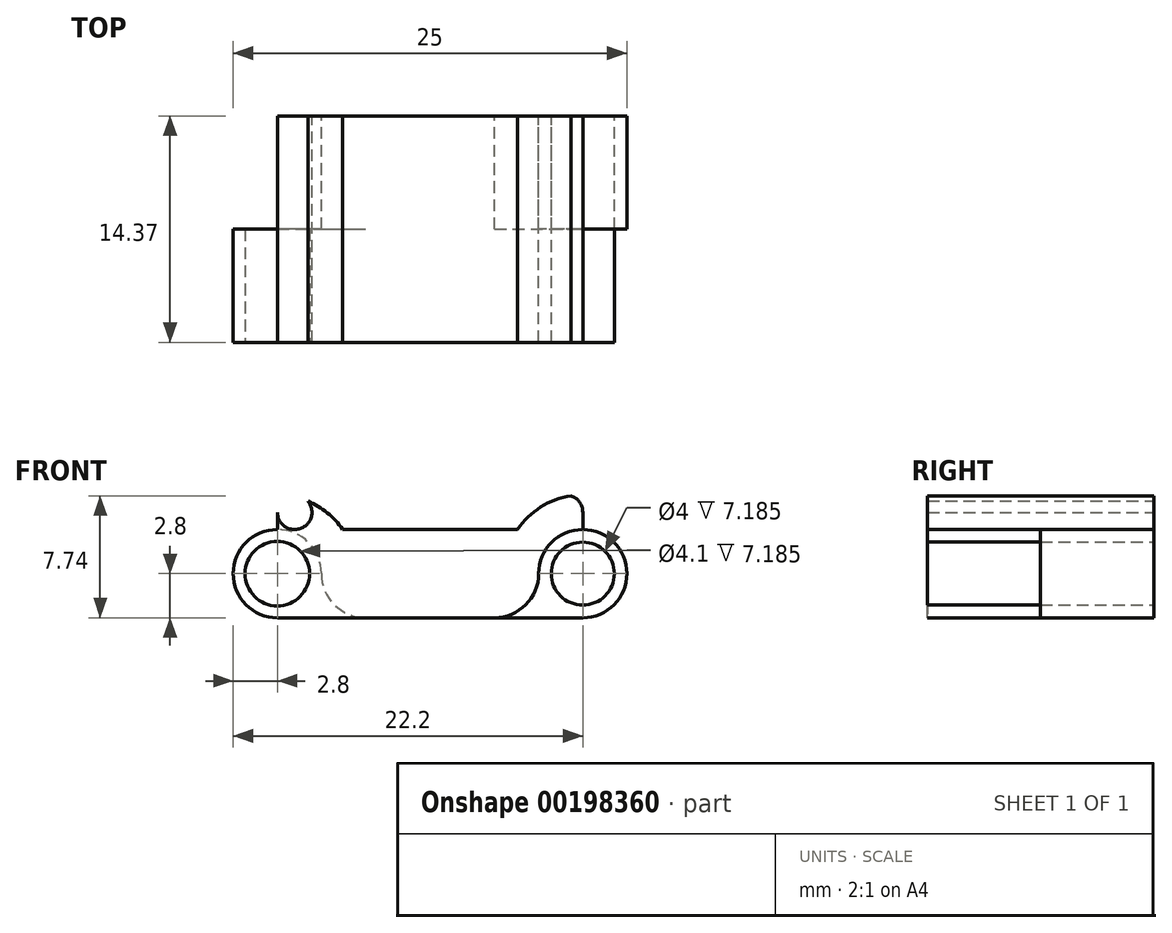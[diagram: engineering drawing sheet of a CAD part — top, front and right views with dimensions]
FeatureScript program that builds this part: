
annotation { "Feature Type Name" : "Feature", "Feature Type Description" : "" }
export const myFeature = defineFeature(function(context is Context, id is Id, definition is map)
    precondition{}
    {
        {
            var Q0;
            Q0=qCreatedBy(makeId("Front.planeOp"),FACE);
            var sketch = newSketch(context, id + "F0", { "sketchPlane" : qUnion([Q0])});
            skLineSegment(sketch, "E0.bottom", {"start": v(2.8, 0) * mm, "end": v(22.2, 0) * mm});
            skLineSegment(sketch, "E0.top", {"start": v(2.8, 5.6) * mm, "end": v(21.1, 5.6) * mm});
            skLineSegment(sketch, "E1.bottom", {"start": v(21.1, 5.6) * mm, "end": v(19.4, 5.6) * mm, "construction": true});
            skLineSegment(sketch, "E1.top", {"start": v(22.2, 0) * mm, "end": v(19.4, 0) * mm, "construction": true});
            skLineSegment(sketch, "E1.right", {"start": v(19.4, 5.6) * mm, "end": v(19.4, 0) * mm, "construction": true});
            skLineSegment(sketch, "E2", {"start": v(19.4, 5.6) * mm, "end": v(25, 0) * mm, "construction": true});
            skCircle(sketch, "E3", {"center": v(22.2, 2.8) * mm, "radius": 2.8 * mm});
            skCircle(sketch, "E4", {"center": v(22.2, 2.8) * mm, "radius": 2 * mm});
            skArc(sketch, "E5", {"start": v(21.45, 7.74) * mm, "mid": v(19.53, 7.03) * mm, "end": v(18.06, 5.6) * mm});
            skArc(sketch, "E6", {"start": v(17.74, 5.05) * mm, "mid": v(20.28, 0.14) * mm, "end": v(19.4, 5.6) * mm, "construction": true});
            skArc(sketch, "E7", {"start": v(16.6, 0) * mm, "mid": v(18.58, 0.82) * mm, "end": v(19.4, 2.8) * mm});
            skLineSegment(sketch, "E8", {"start": v(12.5, 5.6) * mm, "end": v(12.5, 0) * mm, "construction": true});
            skLineSegment(sketch, "E9", {"start": v(22.2, 2.8) * mm, "end": v(22.2, 6.7) * mm, "construction": true});
            skLineSegment(sketch, "E10", {"start": v(22.2, 6.7) * mm, "end": v(22.2, 5.6) * mm});
            skCircle(sketch, "E11", {"center": v(22.2, 6.7) * mm, "radius": 1.1 * mm, "construction": true});
            skArc(sketch, "E12", {"start": v(20.26, 7.4) * mm, "mid": v(21.4, 5.64) * mm, "end": v(21.45, 7.74) * mm});
            skPoint(sketch, "E13.orphan", {"position": v(22.2, 7.8) * mm});
            skPoint(sketch, "E14.orphan", {"position": v(25, 5.6) * mm});
            skArc(sketch, "E15.trimOffspring", {"start": v(17.74, 0.55) * mm, "mid": v(17.8, 0.42) * mm, "end": v(17.87, 0.3) * mm});
            skArc(sketch, "E16.MirrorCS", {"start": v(7.26, 0.55) * mm, "mid": v(7.2, 0.42) * mm, "end": v(7.13, 0.3) * mm});
            skLineSegment(sketch, "E17.MirrorCS", {"start": v(2.8, 6.7) * mm, "end": v(2.8, 5.6) * mm});
            skLineSegment(sketch, "E18.MirrorCS", {"start": v(2.8, 2.8) * mm, "end": v(2.8, 6.7) * mm, "construction": true});
            skCircle(sketch, "E19.MirrorC", {"center": v(2.8, 6.7) * mm, "radius": 1.1 * mm, "construction": true});
            skLineSegment(sketch, "E20.MirrorCS", {"start": v(3.9, 5.6) * mm, "end": v(5.6, 5.6) * mm, "construction": true});
            skPoint(sketch, "E21.MirrorP", {"position": v(0, 5.6) * mm});
            skPoint(sketch, "E22.MirrorP", {"position": v(2.8, 7.8) * mm});
            skLineSegment(sketch, "E23.MirrorCS", {"start": v(2.8, 0) * mm, "end": v(5.6, 0) * mm, "construction": true});
            skLineSegment(sketch, "E24.MirrorCS", {"start": v(5.6, 5.6) * mm, "end": v(0, 0) * mm, "construction": true});
            skLineSegment(sketch, "E25.MirrorCS", {"start": v(5.6, 5.6) * mm, "end": v(5.6, 0) * mm, "construction": true});
            skArc(sketch, "E26.MirrorCS", {"start": v(4.74, 7.4) * mm, "mid": v(3.6, 5.64) * mm, "end": v(3.55, 7.74) * mm});
            skArc(sketch, "E27.MirrorCS", {"start": v(7.26, 5.05) * mm, "mid": v(4.72, 0.14) * mm, "end": v(5.6, 5.6) * mm, "construction": true});
            skArc(sketch, "E28.MirrorCS", {"start": v(3.55, 7.74) * mm, "mid": v(5.47, 7.03) * mm, "end": v(6.94, 5.6) * mm});
            skCircle(sketch, "E29.MirrorC", {"center": v(2.8, 2.8) * mm, "radius": 2.8 * mm});
            skArc(sketch, "E30.MirrorCS", {"start": v(8.4, 0) * mm, "mid": v(6.42, 0.82) * mm, "end": v(5.6, 2.8) * mm});
            skCircle(sketch, "E31.MirrorC", {"center": v(2.8, 2.8) * mm, "radius": 2 * mm});
            skPoint(sketch, "E32.orphan", {"position": v(0, 0) * mm});
            skSolve(sketch);
        }
        {
            var Q0;
            {var subQ0=sQuery(id+"F0.wireOp",EDGE,"E10");Q0=makeQuery(id+"F0.imprint","IMPRINT",FACE,{"disambiguationData":[TD([[makeQuery(id+"F0.imprint","IMPRINT",EDGE,{"derivedFrom":subQ0}),-1.0]])]});}
            var Q1;
            {var subQ0=sQuery(id+"F0.wireOp",EDGE,"E12");var subQ1=sQuery(id+"F0.wireOp",EDGE,"E0.top");var subQ2=makeQuery(id+"F0.imprint","INTERSECT",VERTEX,{"derivedFrom":[subQ1,subQ0]});Q1=makeQuery(id+"F0.imprint","IMPRINT",FACE,{"disambiguationData":[TD([[makeQuery(id+"F0.imprint","IMPRINT",EDGE,{"disambiguationData":[TD([[subQ2,1.0]])],"derivedFrom":subQ1}),1.0]])]});}
            var Q2;
            {var subQ0=sQuery(id+"F0.wireOp",EDGE,"E12");var subQ1=sQuery(id+"F0.wireOp",EDGE,"E5");var subQ2=makeQuery(id+"F0.imprint","INTERSECT",VERTEX,{"disambiguationData":[OD(0.0)],"derivedFrom":[subQ1,subQ0]});Q2=makeQuery(id+"F0.imprint","IMPRINT",FACE,{"disambiguationData":[TD([[makeQuery(id+"F0.imprint","IMPRINT",EDGE,{"disambiguationData":[TD([[subQ2,-1.0]])],"derivedFrom":subQ1}),1.0]])]});}
            var Q3;
            {var subQ0=sQuery(id+"F0.wireOp",EDGE,"E28.MirrorCS");var subQ1=sQuery(id+"F0.wireOp",EDGE,"E0.top");var subQ2=makeQuery(id+"F0.imprint","INTERSECT",VERTEX,{"derivedFrom":[subQ1,subQ0]});Q3=makeQuery(id+"F0.imprint","IMPRINT",FACE,{"disambiguationData":[TD([[makeQuery(id+"F0.imprint","IMPRINT",EDGE,{"disambiguationData":[TD([[subQ2,1.0]])],"derivedFrom":subQ1}),1.0]])]});}
            var Q4;
            {var subQ0=sQuery(id+"F0.wireOp",EDGE,"E28.MirrorCS");var subQ1=sQuery(id+"F0.wireOp",EDGE,"E26.MirrorCS");var subQ2=makeQuery(id+"F0.imprint","INTERSECT",VERTEX,{"disambiguationData":[OD(0.0)],"derivedFrom":[subQ1,subQ0]});Q4=makeQuery(id+"F0.imprint","IMPRINT",FACE,{"disambiguationData":[TD([[makeQuery(id+"F0.imprint","IMPRINT",EDGE,{"disambiguationData":[TD([[subQ2,-1.0]])],"derivedFrom":subQ1}),-1.0]])]});}
            var Q5;
            {var subQ0=sQuery(id+"F0.wireOp",EDGE,"E17.MirrorCS");Q5=makeQuery(id+"F0.imprint","IMPRINT",FACE,{"disambiguationData":[TD([[makeQuery(id+"F0.imprint","IMPRINT",EDGE,{"derivedFrom":subQ0}),1.0]])]});}
            var Q6;
            Q6=makeQuery(id+"F0.imprint","IMPRINT",FACE,{"disambiguationData":[TD([[makeQuery(id+"F0.imprint","IMPRINT",EDGE,{"derivedFrom":sQuery(id+"F0.wireOp",EDGE,"E4")}),1.0]])]});
            extrude(context, id + "F1", {"entities" : qUnion([Q0, Q1, Q2, Q3, Q4, Q5, Q6]), "depth" : 14.37 * mm});
        }
        {
            var Q0;
            Q0=makeQuery(id+"F0.imprint","IMPRINT",FACE,{"disambiguationData":[TD([[makeQuery(id+"F0.imprint","IMPRINT",EDGE,{"derivedFrom":sQuery(id+"F0.wireOp",EDGE,"E4")}),-1.0]])]});
            var Q1;
            {var subQ3=sQuery(id+"F0.wireOp",EDGE,"E7");var subQ6=makeQuery(id+"F0.imprint","IMPRINT",VERTEX,{"derivedFrom":subQ3});Q1=makeQuery(id+"F0.imprint","IMPRINT",FACE,{"disambiguationData":[TD([[makeQuery(id+"F0.imprint","IMPRINT",EDGE,{"disambiguationData":[TD([[subQ6,1.0]])],"derivedFrom":subQ3}),-1.0]])]});}
            extrude(context, id + "F2", {"entities" : qUnion([Q0, Q1]), "depth" : 7.18 * mm});
        }
        {
            var Q0;
            Q0=makeQuery(id+"F1.opExtrude","CAP_FACE",FACE,{"disambiguationData":[OSD([sQuery(id+"F0.wireOp",EDGE,"E0.bottom"),sQuery(id+"F0.wireOp",EDGE,"E0.top"),sQuery(id+"F0.wireOp",EDGE,"E3"),sQuery(id+"F0.wireOp",EDGE,"E5"),sQuery(id+"F0.wireOp",EDGE,"E7"),sQuery(id+"F0.wireOp",EDGE,"E10"),sQuery(id+"F0.wireOp",EDGE,"E12"),sQuery(id+"F0.wireOp",EDGE,"E17.MirrorCS"),sQuery(id+"F0.wireOp",EDGE,"E26.MirrorCS"),sQuery(id+"F0.wireOp",EDGE,"E28.MirrorCS"),sQuery(id+"F0.wireOp",EDGE,"E29.MirrorC"),sQuery(id+"F0.wireOp",EDGE,"E30.MirrorCS")])],"isStart":false});
            var sketch = newSketch(context, id + "F3", { "sketchPlane" : qUnion([Q0])});
            skLineSegment(sketch, "E33", {"start": v(5.6, 2.8) * mm, "end": v(2.8, 2.8) * mm, "construction": true});
            skCircle(sketch, "E34", {"center": v(2.8, 2.8) * mm, "radius": 2.8 * mm});
            skCircle(sketch, "E35", {"center": v(2.8, 2.8) * mm, "radius": 2.05 * mm});
            skCircle(sketch, "E36", {"center": v(8.4, 2.8) * mm, "radius": 2.8 * mm});
            skLineSegment(sketch, "E37", {"start": v(2.8, 0) * mm, "end": v(8.4, 0) * mm});
            skSolve(sketch);
        }
        {
            var Q0;
            Q0=makeQuery(id+"F3.imprint","IMPRINT",FACE,{"disambiguationData":[TD([[makeQuery(id+"F3.imprint","IMPRINT",EDGE,{"derivedFrom":sQuery(id+"F3.wireOp",EDGE,"E35")}),-1.0]])]});
            var Q1;
            {var subQ3=sQuery(id+"F3.wireOp",EDGE,"E37");Q1=makeQuery(id+"F3.imprint","IMPRINT",FACE,{"disambiguationData":[TD([[makeQuery(id+"F3.imprint","IMPRINT",EDGE,{"derivedFrom":subQ3}),1.0]])]});}
            extrude(context, id + "F4", {"entities" : qUnion([Q0, Q1]), "operationType" : NewBodyOperationType.ADD, "oppositeDirection" : true, "depth" : 7.18 * mm});
        }
    });
